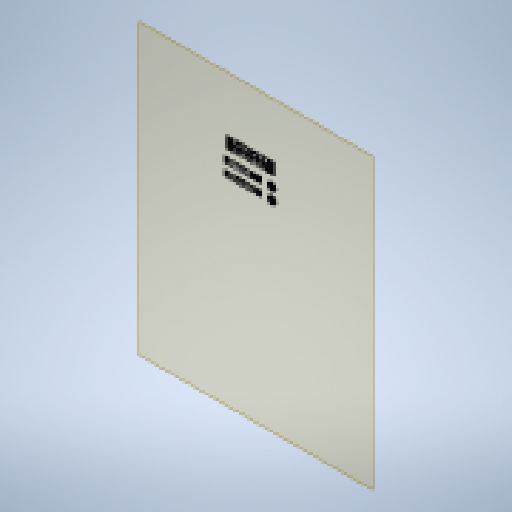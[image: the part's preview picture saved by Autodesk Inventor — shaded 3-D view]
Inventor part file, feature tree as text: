
AUTODESK INVENTOR PART (.ipt)
format: ipt  version: 2023 (Build 270158030, 158C)  size: 229,376 bytes
history: native  units: mm
features: other x9, sketch x4, plane x1, extrude x1
ambient origin geometry x8: Origin, YZ Plane, XZ Plane, XY Plane, X Axis, Y Axis, Z Axis, Center Point
bodies: Solid1 (feature_tree)
feature tree (15):
  plane  "Work Plane1"
  extrude  "Extrusion1"  Depth=12.0mm
  other  "Decal1"
  other  "Decal2"
  other  "Decal3"
  sketch  "Sketch1"  dims[d0=70.0mm d1=12.0mm]
  sketch  "Sketch2"  dims[d2=70.0mm d3=12.0mm]
  other  "Image1"
  sketch  "Sketch3"  dims[d4=16.0mm]
  other  "Image2"
  sketch  "Sketch5"  dims[d5=20.0mm d8=20.0mm d9=1.0mm d10=0.0mm d11=23.0mm d12=90.0mm d13=5.0mm d40=1.0mm d41=1.0mm d42=13.0mm d58=0.7mm d59=10.0mm d60=0.7mm d62=0.7mm d65=0.7mm d66=10.0mm]
  other  "Image3"
  other  "<userpath>\Documents\0004-inventor\Inventor_Projects\electronics-enclosure\enclosure.iam"
  other  "enclosure.iam"
  other  "door:1"
